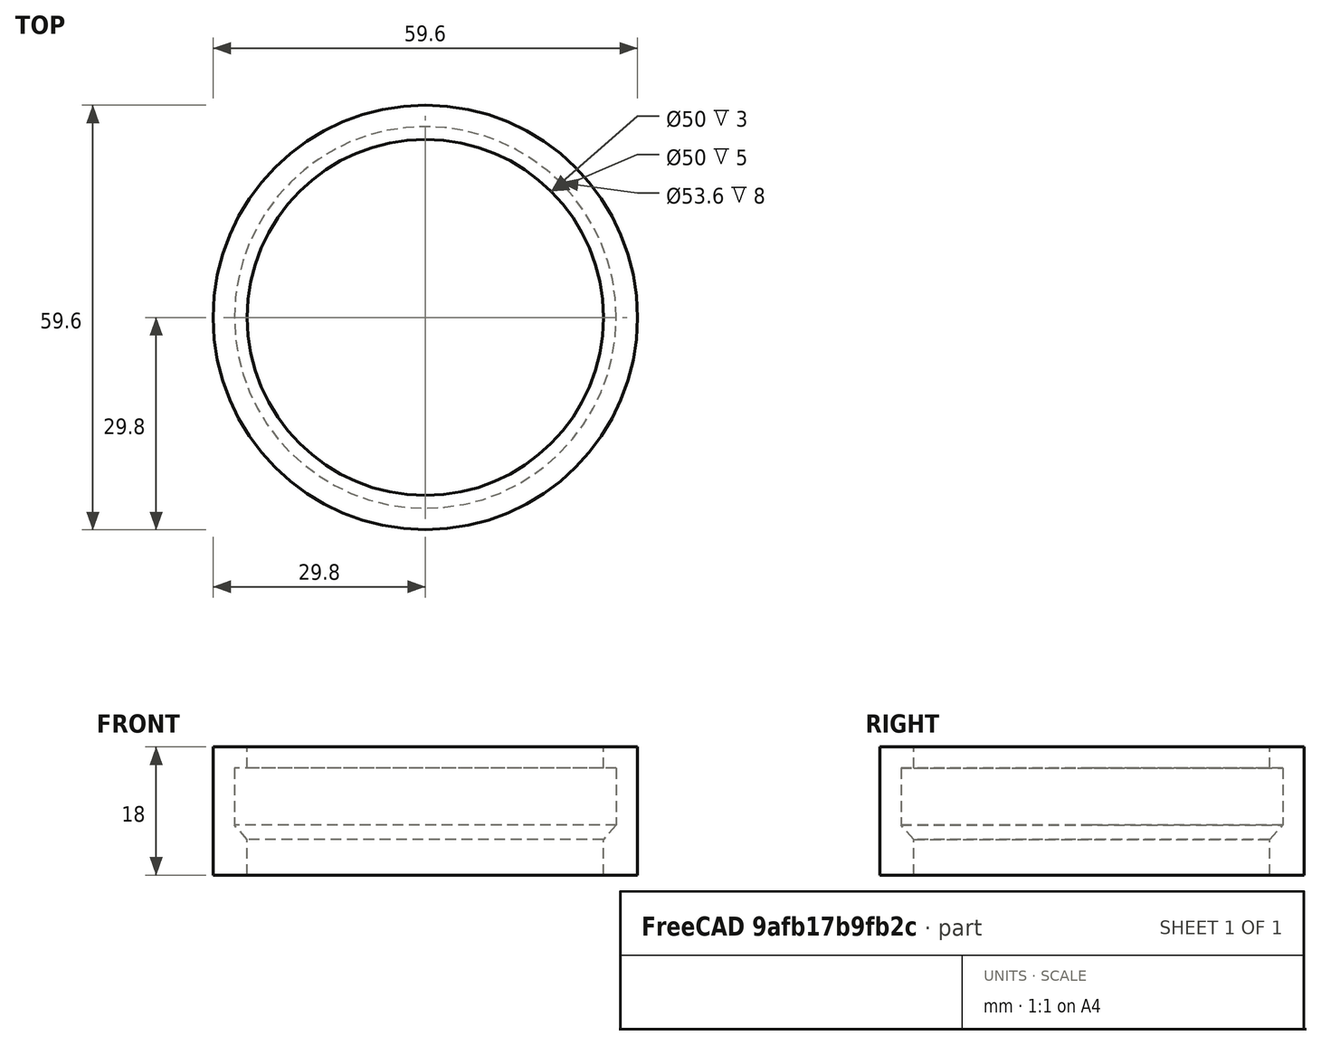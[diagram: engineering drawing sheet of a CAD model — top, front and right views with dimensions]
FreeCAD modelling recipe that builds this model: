
FCSTD DOCUMENT  (FreeCAD 1.1R39748 (Git))
Label: горло
License: All rights reserved
LicenseURL: https://en.wikipedia.org/wiki/All_rights_reserved
objects: App::Point×1, Sketcher::SketchObject×1, PartDesign::Revolution×1, PartDesign::Body×1
note: 6 computed .brp shape members not serialized (recipe doc carries the construction recipe); baked Part::Feature solids carry a one-line shape summary decoded from their .brp

FEATURE [App::Point] Origin001
  Role = Origin
FEATURE [Sketcher::SketchObject] Sketch
  ArcFitTolerance = 1e-06
  AttachmentSupport = -> [XZ_Plane]
  ExternalTypes = [0]
  FullyConstrained = true
  MakeInternals = false
  MapMode = 5
  Placement = pos=(0,0,0) rot=(1,0,0;1.5708rad)
  expr: Constraints[23] = 63 / 2 - 1.8
  expr: Constraints[2] = 50 / 2
  sketch-geometry (8):
    g0: LineSegment StartX=25 StartY=0 StartZ=0 EndX=25 EndY=5 EndZ=0
    g1: LineSegment StartX=29.7 StartY=17.7 StartZ=0 EndX=29.7 EndY=9.7 EndZ=0
    g2: LineSegment StartX=29.7 StartY=9.7 StartZ=0 EndX=25 EndY=5 EndZ=0
    g3: LineSegment StartX=29.7 StartY=17.7 StartZ=0 EndX=25 EndY=17.7 EndZ=0
    g4: LineSegment StartX=25 StartY=17.7 StartZ=0 EndX=25 EndY=20.7 EndZ=0
    g5: LineSegment StartX=25 StartY=20.7 StartZ=0 EndX=32.7 EndY=20.7 EndZ=0
    g6: LineSegment StartX=32.7 StartY=20.7 StartZ=0 EndX=32.7 EndY=0 EndZ=0
    g7: LineSegment StartX=32.7 StartY=0 StartZ=0 EndX=25 EndY=0 EndZ=0
  constraints (25):
    c: PointOnObject(g0,g-1)
    c: Vertical(g0)
    c: Distance(g0,g-1) = 25
    c: Vertical(g1)
    c: Coincident(g2,g0)
    c: Coincident(g1,g2)
    c: Distance(g1,g1) = 8
    c: Coincident(g3,g1)
    c: Horizontal(g3)
    c: DistanceX(g-1,g3) = 25
    c: Coincident(g4,g3)
    c: Vertical(g4)
    c: Coincident(g5,g4)
    c: Horizontal(g5)
    c: Coincident(g6,g5)
    c: PointOnObject(g6,g-1)
    c: Vertical(g6)
    c: Coincident(g7,g6)
    c: Coincident(g7,g0)
    c: Distance(g3,g4) = 3
    c: DistanceX(g1,g6) = 3
    c: DistanceY(g0,g0) = 5
    c: Angle(g0,g2) = 2.35619
    c: DistanceX(g-1,g1) = 29.7
    c: Distance(g3,g1) = 4.7
FEATURE [PartDesign::Revolution] Revolution
  Angle = 360
  Angle2 = 60
  Axis = (0,2e-16,1)
  Base = (0,0,0)
  Placement = pos=(0,0,0) rot=(1,0,0;1.5708rad)
  Profile = -> Sketch
  ReferenceAxis = -> Sketch [V_Axis]
  Reversed = true
  Suppressed = false
  Type = 0
FEATURE [PartDesign::Body] Body
  AllowCompound = false
  Group = -> [Sketch,Revolution]
  Origin = -> Origin
  Tip = -> Revolution
